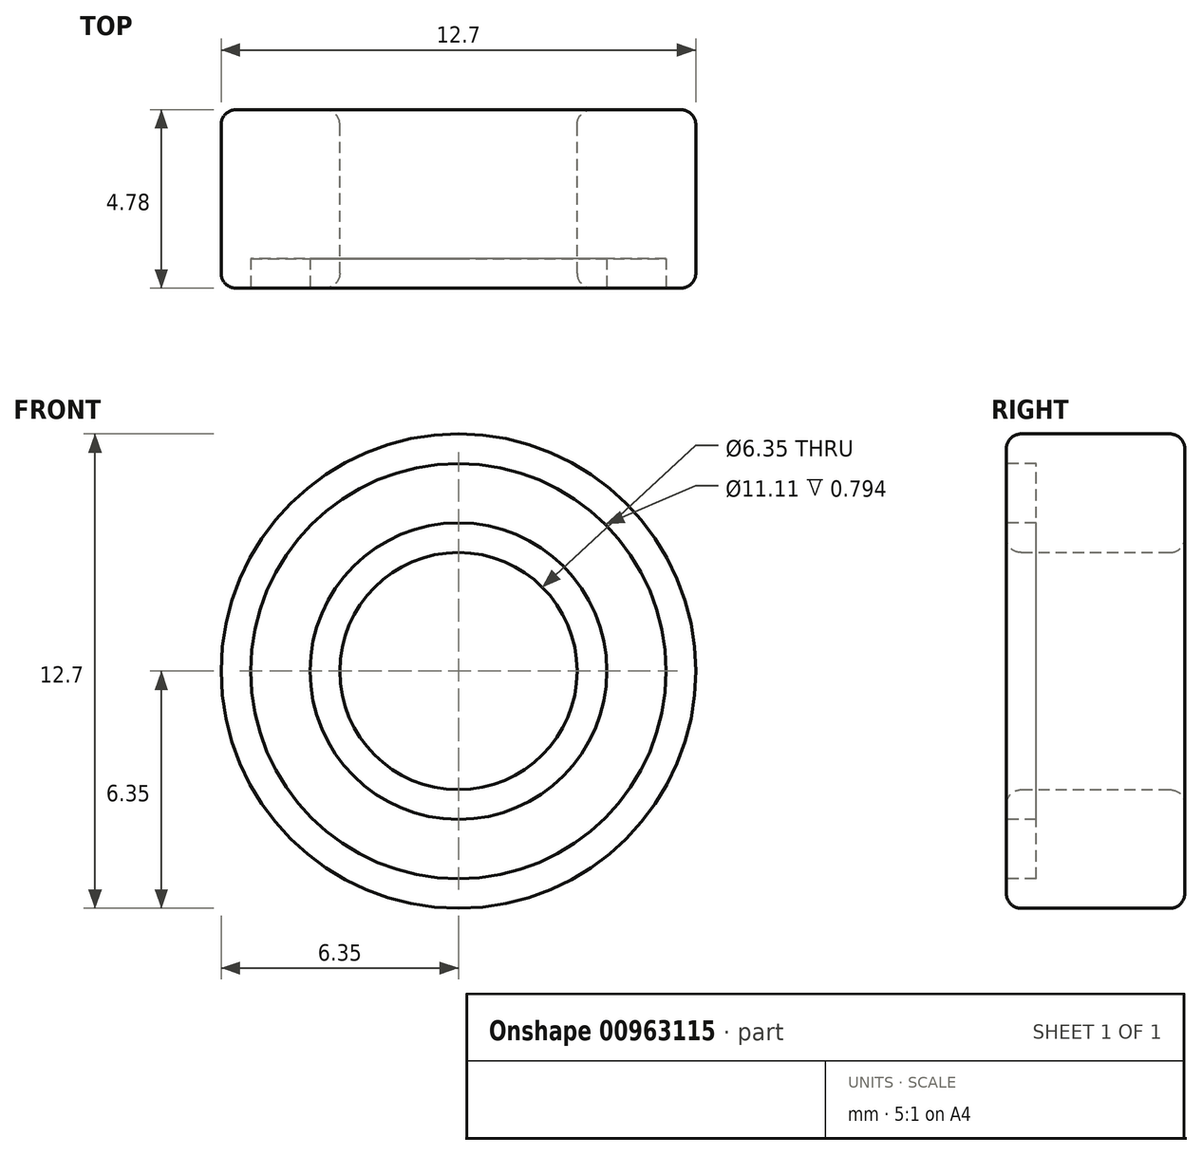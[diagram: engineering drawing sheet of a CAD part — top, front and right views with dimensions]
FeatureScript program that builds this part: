
annotation { "Feature Type Name" : "Feature", "Feature Type Description" : "" }
export const myFeature = defineFeature(function(context is Context, id is Id, definition is map)
    precondition{}
    {
        {
            var Q0;
            Q0=qCreatedBy(makeId("Front.planeOp"),FACE);
            var sketch = newSketch(context, id + "F0", { "sketchPlane" : qUnion([Q0])});
            skCircle(sketch, "E0", {"center": v(0, 0) * mm, "radius": 3.18 * mm});
            skCircle(sketch, "E1", {"center": v(0, 0) * mm, "radius": 6.35 * mm});
            skSolve(sketch);
        }
        {
            var Q0;
            Q0 = qSketchRegion(id + "F0", true);
            extrude(context, id + "F1", {"entities" : qUnion([Q0]), "depth" : (25.4 * 0.19) * mm, "offsetDistance" : 25 * mm, "symmetric" : true});
        }
        {
            var Q0;
            Q0=makeQuery(id+"F1.opExtrude","CAP_FACE",FACE,{"disambiguationData":[OSD([sQuery(id+"F0.wireOp",EDGE,"E0"),sQuery(id+"F0.wireOp",EDGE,"E1")])],"isStart":false});
            var sketch = newSketch(context, id + "F2", { "sketchPlane" : qUnion([Q0])});
            skCircle(sketch, "E2", {"center": v(0, 0) * mm, "radius": 3.97 * mm});
            skCircle(sketch, "E3", {"center": v(0, 0) * mm, "radius": 5.56 * mm});
            skSolve(sketch);
        }
        {
            var Q0;
            Q0=makeQuery(id+"F2.imprint","IMPRINT",FACE,{"disambiguationData":[TD([[makeQuery(id+"F2.imprint","IMPRINT",EDGE,{"derivedFrom":sQuery(id+"F2.wireOp",EDGE,"E2")}),-1.0]])]});
            extrude(context, id + "F3", {"entities" : qUnion([Q0]), "operationType" : NewBodyOperationType.REMOVE, "oppositeDirection" : true, "depth" : (25.4 / 32) * mm, "offsetDistance" : 25 * mm});
        }
        {
            var Q0;
            Q0=makeQuery(id+"F1.opExtrude","SWEPT_FACE",FACE,{"disambiguationData":[OSD([sQuery(id+"F0.wireOp",EDGE,"E0")])]});
            var Q1;
            Q1=makeQuery(id+"F1.opExtrude","SWEPT_FACE",FACE,{"disambiguationData":[OSD([sQuery(id+"F0.wireOp",EDGE,"E1")])]});
            fillet(context, id + "F4", {"entities" : qUnion([Q0, Q1]), "radius" : (25.4 / 64) * mm, "tangentPropagation" : true, "allowEdgeOverflow" : false});
        }
    });
